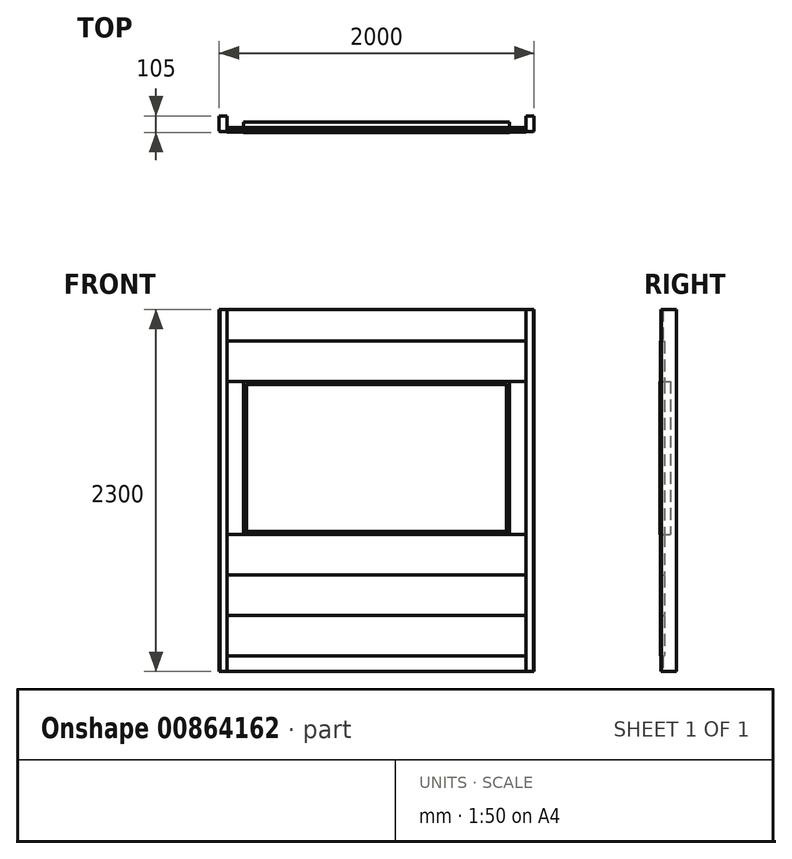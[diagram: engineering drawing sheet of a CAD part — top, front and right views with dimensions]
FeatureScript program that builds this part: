
annotation { "Feature Type Name" : "Feature", "Feature Type Description" : "" }
export const myFeature = defineFeature(function(context is Context, id is Id, definition is map)
    precondition{}
    {
        {
            var Q0;
            Q0=qCreatedBy(makeId("Front.planeOp"),FACE);
            var sketch = newSketch(context, id + "F0", { "sketchPlane" : qUnion([Q0])});
            skLineSegment(sketch, "E0.bottom", {"start": v(-1000, 2300) * mm, "end": v(-950, 2300) * mm});
            skLineSegment(sketch, "E0.top", {"start": v(-1000, 0) * mm, "end": v(-950, 0) * mm});
            skLineSegment(sketch, "E0.left", {"start": v(-1000, 2300) * mm, "end": v(-1000, 0) * mm});
            skLineSegment(sketch, "E0.right", {"start": v(-950, 2300) * mm, "end": v(-950, 0) * mm});
            skLineSegment(sketch, "E1.bottom", {"start": v(950, 2300) * mm, "end": v(1000, 2300) * mm});
            skLineSegment(sketch, "E1.top", {"start": v(950, 0) * mm, "end": v(1000, 0) * mm});
            skLineSegment(sketch, "E1.left", {"start": v(950, 2300) * mm, "end": v(950, 0) * mm});
            skLineSegment(sketch, "E1.right", {"start": v(1000, 2300) * mm, "end": v(1000, 0) * mm});
            skLineSegment(sketch, "E2.bottom", {"start": v(-950, 0) * mm, "end": v(950, 0) * mm});
            skLineSegment(sketch, "E2.top", {"start": v(-950, 100) * mm, "end": v(950, 100) * mm});
            skLineSegment(sketch, "E2.left", {"start": v(-950, 0) * mm, "end": v(-950, 100) * mm});
            skLineSegment(sketch, "E2.right", {"start": v(950, 0) * mm, "end": v(950, 100) * mm});
            skLineSegment(sketch, "E3.bottom", {"start": v(950, 2300) * mm, "end": v(-950, 2300) * mm});
            skLineSegment(sketch, "E3.top", {"start": v(950, 2100) * mm, "end": v(-950, 2100) * mm});
            skLineSegment(sketch, "E3.left", {"start": v(950, 2300) * mm, "end": v(950, 2100) * mm});
            skLineSegment(sketch, "E3.right", {"start": v(-950, 2300) * mm, "end": v(-950, 2100) * mm});
            skLineSegment(sketch, "E4.bottom", {"start": v(-844.5, 1843.25) * mm, "end": v(844.5, 1843.25) * mm});
            skLineSegment(sketch, "E4.top", {"start": v(-844.5, 870.25) * mm, "end": v(844.5, 870.25) * mm});
            skLineSegment(sketch, "E4.left", {"start": v(-844.5, 1843.25) * mm, "end": v(-844.5, 870.25) * mm});
            skLineSegment(sketch, "E4.right", {"start": v(844.5, 1843.25) * mm, "end": v(844.5, 870.25) * mm});
            skLineSegment(sketch, "E5", {"start": v(0, 1843.25) * mm, "end": v(0, 2100) * mm, "construction": true});
            skLineSegment(sketch, "E6", {"start": v(-844.5, 1843.25) * mm, "end": v(-950, 1843.25) * mm});
            skLineSegment(sketch, "E7", {"start": v(844.5, 1843.25) * mm, "end": v(950, 1843.25) * mm});
            skLineSegment(sketch, "E8", {"start": v(-844.5, 870.25) * mm, "end": v(-950, 870.25) * mm});
            skLineSegment(sketch, "E9", {"start": v(844.5, 870.25) * mm, "end": v(950, 870.25) * mm});
            skPoint(sketch, "E9.endSnap0", {"position": v(950, 1150) * mm});
            skLineSegment(sketch, "E10", {"start": v(0, 870.25) * mm, "end": v(0, 613.5) * mm, "construction": true});
            skLineSegment(sketch, "E11", {"start": v(0, 613.5) * mm, "end": v(0, 356.75) * mm, "construction": true});
            skLineSegment(sketch, "E12", {"start": v(0, 356.75) * mm, "end": v(0, 100) * mm, "construction": true});
            skLineSegment(sketch, "E13", {"start": v(-950, 613.5) * mm, "end": v(950, 613.5) * mm});
            skLineSegment(sketch, "E14", {"start": v(-950, 356.75) * mm, "end": v(950, 356.75) * mm});
            skLineSegment(sketch, "E15.bottom", {"start": v(-824.5, 1823.25) * mm, "end": v(824.5, 1823.25) * mm});
            skLineSegment(sketch, "E15.top", {"start": v(-824.5, 890.25) * mm, "end": v(824.5, 890.25) * mm});
            skLineSegment(sketch, "E15.left", {"start": v(-824.5, 1823.25) * mm, "end": v(-824.5, 890.25) * mm});
            skLineSegment(sketch, "E15.right", {"start": v(824.5, 1823.25) * mm, "end": v(824.5, 890.25) * mm});
            skLineSegment(sketch, "E16", {"start": v(0, 1843.25) * mm, "end": v(0, 1823.25) * mm, "construction": true});
            skLineSegment(sketch, "E17", {"start": v(-824.5, 1356.75) * mm, "end": v(-844.5, 1356.75) * mm, "construction": true});
            skSolve(sketch);
        }
        {
            var Q0;
            Q0=makeQuery(id+"F0.imprint","IMPRINT",FACE,{"disambiguationData":[TD([[makeQuery(id+"F0.imprint","IMPRINT",EDGE,{"derivedFrom":sQuery(id+"F0.wireOp",EDGE,"E0.bottom")}),-1.0]])]});
            var Q1;
            Q1=makeQuery(id+"F0.imprint","IMPRINT",FACE,{"disambiguationData":[TD([[makeQuery(id+"F0.imprint","IMPRINT",EDGE,{"derivedFrom":sQuery(id+"F0.wireOp",EDGE,"E1.bottom")}),-1.0]])]});
            extrude(context, id + "F1", {"entities" : qUnion([Q0, Q1]), "oppositeDirection" : true, "depth" : 100 * mm, "offsetDistance" : 25 * mm});
        }
        {
            var Q0;
            Q0=makeQuery(id+"F0.imprint","IMPRINT",FACE,{"disambiguationData":[TD([[makeQuery(id+"F0.imprint","IMPRINT",EDGE,{"derivedFrom":sQuery(id+"F0.wireOp",EDGE,"E3.bottom")}),1.0]])]});
            var Q1;
            Q1=makeQuery(id+"F0.imprint","IMPRINT",FACE,{"disambiguationData":[TD([[makeQuery(id+"F0.imprint","IMPRINT",EDGE,{"derivedFrom":sQuery(id+"F0.wireOp",EDGE,"E2.bottom")}),1.0]])]});
            extrude(context, id + "F2", {"entities" : qUnion([Q0, Q1]), "oppositeDirection" : true, "depth" : 15 * mm, "offsetDistance" : 25 * mm});
        }
        {
            var Q0;
            {var subQ0=sQuery(id+"F0.wireOp",EDGE,"E3.top");Q0=makeQuery(id+"F0.imprint","IMPRINT",FACE,{"disambiguationData":[TD([[makeQuery(id+"F0.imprint","IMPRINT",EDGE,{"derivedFrom":subQ0}),1.0]])]});}
            var Q1;
            Q1=makeQuery(id+"F0.imprint","IMPRINT",FACE,{"disambiguationData":[TD([[makeQuery(id+"F0.imprint","IMPRINT",EDGE,{"derivedFrom":sQuery(id+"F0.wireOp",EDGE,"E4.top")}),-1.0]])]});
            var Q2;
            {var subQ0=sQuery(id+"F0.wireOp",EDGE,"E2.top");Q2=makeQuery(id+"F0.imprint","IMPRINT",FACE,{"disambiguationData":[TD([[makeQuery(id+"F0.imprint","IMPRINT",EDGE,{"derivedFrom":subQ0}),1.0]])]});}
            extrude(context, id + "F3", {"entities" : qUnion([Q0, Q1, Q2]), "depth" : 3 * mm, "offsetDistance" : 25 * mm, "hasSecondDirection" : true, "secondDirectionOppositeDirection" : true, "secondDirectionDepth" : 25 * mm});
        }
        {
            var Q0;
            Q0=makeQuery(id+"F0.imprint","IMPRINT",FACE,{"disambiguationData":[TD([[makeQuery(id+"F0.imprint","IMPRINT",EDGE,{"derivedFrom":sQuery(id+"F0.wireOp",EDGE,"E4.left")}),-1.0]])]});
            var Q1;
            Q1=makeQuery(id+"F0.imprint","IMPRINT",FACE,{"disambiguationData":[TD([[makeQuery(id+"F0.imprint","IMPRINT",EDGE,{"derivedFrom":sQuery(id+"F0.wireOp",EDGE,"E4.right")}),1.0]])]});
            var Q2;
            {var subQ0=sQuery(id+"F0.wireOp",EDGE,"E13");Q2=makeQuery(id+"F0.imprint","IMPRINT",FACE,{"disambiguationData":[TD([[makeQuery(id+"F0.imprint","IMPRINT",EDGE,{"derivedFrom":subQ0}),-1.0]])]});}
            extrude(context, id + "F4", {"entities" : qUnion([Q0, Q1, Q2]), "depth" : 3 * mm, "offsetDistance" : 25 * mm, "hasSecondDirection" : true, "secondDirectionOppositeDirection" : true, "secondDirectionDepth" : 25 * mm});
        }
        {
            var Q0;
            Q0=makeQuery(id+"F0.imprint","IMPRINT",FACE,{"disambiguationData":[TD([[makeQuery(id+"F0.imprint","IMPRINT",EDGE,{"derivedFrom":sQuery(id+"F0.wireOp",EDGE,"E4.bottom")}),-1.0]])]});
            var Q1;
            Q1=makeQuery(id+"F0.imprint","IMPRINT",FACE,{"disambiguationData":[TD([[makeQuery(id+"F0.imprint","IMPRINT",EDGE,{"derivedFrom":sQuery(id+"F0.wireOp",EDGE,"E15.bottom")}),-1.0]])]});
            extrude(context, id + "F5", {"entities" : qUnion([Q0, Q1]), "depth" : 5 * mm, "offsetDistance" : 25 * mm, "hasSecondDirection" : true, "secondDirectionOppositeDirection" : true, "secondDirectionDepth" : 60 * mm});
        }
        {
            var Q0;
            Q0=makeQuery(id+"F0.imprint","IMPRINT",FACE,{"disambiguationData":[TD([[makeQuery(id+"F0.imprint","IMPRINT",EDGE,{"derivedFrom":sQuery(id+"F0.wireOp",EDGE,"E15.bottom")}),-1.0]])]});
            extrude(context, id + "F6", {"entities" : qUnion([Q0]), "operationType" : NewBodyOperationType.REMOVE, "depth" : 25 * mm, "offsetDistance" : 25 * mm});
        }
        {
            var Q0;
            Q0=makeQuery(id+"F6.boolean.opBoolean","INTERSECT",EDGE,{"derivedFrom":[makeQuery(id+"F5.opExtrude","CAP_FACE",FACE,{"disambiguationData":[OSD([sQuery(id+"F0.wireOp",EDGE,"E4.bottom"),sQuery(id+"F0.wireOp",EDGE,"E4.top"),sQuery(id+"F0.wireOp",EDGE,"E4.left"),sQuery(id+"F0.wireOp",EDGE,"E4.right")])],"isStart":false}),makeQuery(id+"F6.opExtrude","SWEPT_FACE",FACE,{"disambiguationData":[OSD([sQuery(id+"F0.wireOp",EDGE,"E15.bottom")])]})]});
            var Q1;
            Q1=makeQuery(id+"F6.boolean.opBoolean","INTERSECT",EDGE,{"derivedFrom":[makeQuery(id+"F5.opExtrude","CAP_FACE",FACE,{"disambiguationData":[OSD([sQuery(id+"F0.wireOp",EDGE,"E4.bottom"),sQuery(id+"F0.wireOp",EDGE,"E4.top"),sQuery(id+"F0.wireOp",EDGE,"E4.left"),sQuery(id+"F0.wireOp",EDGE,"E4.right")])],"isStart":false}),makeQuery(id+"F6.opExtrude","SWEPT_FACE",FACE,{"disambiguationData":[OSD([sQuery(id+"F0.wireOp",EDGE,"E15.left")])]})]});
            var Q2;
            Q2=makeQuery(id+"F6.boolean.opBoolean","INTERSECT",EDGE,{"derivedFrom":[makeQuery(id+"F5.opExtrude","CAP_FACE",FACE,{"disambiguationData":[OSD([sQuery(id+"F0.wireOp",EDGE,"E4.bottom"),sQuery(id+"F0.wireOp",EDGE,"E4.top"),sQuery(id+"F0.wireOp",EDGE,"E4.left"),sQuery(id+"F0.wireOp",EDGE,"E4.right")])],"isStart":false}),makeQuery(id+"F6.opExtrude","SWEPT_FACE",FACE,{"disambiguationData":[OSD([sQuery(id+"F0.wireOp",EDGE,"E15.right")])]})]});
            var Q3;
            Q3=makeQuery(id+"F6.boolean.opBoolean","INTERSECT",EDGE,{"derivedFrom":[makeQuery(id+"F5.opExtrude","CAP_FACE",FACE,{"disambiguationData":[OSD([sQuery(id+"F0.wireOp",EDGE,"E4.bottom"),sQuery(id+"F0.wireOp",EDGE,"E4.top"),sQuery(id+"F0.wireOp",EDGE,"E4.left"),sQuery(id+"F0.wireOp",EDGE,"E4.right")])],"isStart":false}),makeQuery(id+"F6.opExtrude","SWEPT_FACE",FACE,{"disambiguationData":[OSD([sQuery(id+"F0.wireOp",EDGE,"E15.top")])]})]});
            var Q4;
            Q4=makeQuery(id+"F1.opExtrude","CAP_EDGE",EDGE,{"disambiguationData":[OSD([sQuery(id+"F0.wireOp",EDGE,"E0.left")])],"isStart":true});
            var Q5;
            Q5=makeQuery(id+"F1.opExtrude","CAP_EDGE",EDGE,{"disambiguationData":[OSD([sQuery(id+"F0.wireOp",EDGE,"E1.right")])],"isStart":true});
            chamfer(context, id + "F7", {"entities" : qUnion([Q0, Q1, Q2, Q3, Q4, Q5]), "width" : 5 * mm, "tangentPropagation" : true});
        }
        {
            var Q0;
            Q0=makeQuery(id+"F4.opExtrude","CAP_EDGE",EDGE,{"disambiguationData":[OSD([sQuery(id+"F0.wireOp",EDGE,"E4.right")])],"isStart":false});
            var Q1;
            Q1=makeQuery(id+"F3.opExtrude","CAP_EDGE",EDGE,{"disambiguationData":[OSD([sQuery(id+"F0.wireOp",EDGE,"E3.top")])],"isStart":true});
            var Q2;
            Q2=makeQuery(id+"F4.opExtrude","SWEPT_EDGE",EDGE,{"disambiguationData":[OSD([sQuery(id+"F0.wireOp",EDGE,"E4.bottom"),sQuery(id+"F0.wireOp",EDGE,"E4.right"),sQuery(id+"F0.wireOp",EDGE,"E7")])]});
            var Q3;
            Q3=makeQuery(id+"F4.opExtrude","CAP_EDGE",EDGE,{"disambiguationData":[OSD([sQuery(id+"F0.wireOp",EDGE,"E9")])],"isStart":false});
            var Q4;
            Q4=makeQuery(id+"F4.opExtrude","SWEPT_EDGE",EDGE,{"disambiguationData":[OSD([sQuery(id+"F0.wireOp",EDGE,"E4.top"),sQuery(id+"F0.wireOp",EDGE,"E4.right"),sQuery(id+"F0.wireOp",EDGE,"E9")])]});
            var Q5;
            {var subQ0=sQuery(id+"F0.wireOp",EDGE,"E1.left");Q5=makeQuery(id+"F4.opExtrude","CAP_EDGE",EDGE,{"disambiguationData":[OSD([subQ0]),TDD([makeQuery(id+"F0.imprint","IMPRINT",EDGE,{"disambiguationData":[TD([[makeQuery(id+"F0.imprint","INTERSECT",VERTEX,{"derivedFrom":[subQ0,sQuery(id+"F0.wireOp",EDGE,"E7")]}),-1.0]])],"derivedFrom":subQ0})])],"isStart":false});}
            var Q6;
            Q6=makeQuery(id+"F4.opExtrude","SWEPT_EDGE",EDGE,{"disambiguationData":[OSD([sQuery(id+"F0.wireOp",EDGE,"E4.bottom"),sQuery(id+"F0.wireOp",EDGE,"E4.left"),sQuery(id+"F0.wireOp",EDGE,"E6")])]});
            var Q7;
            {var subQ0=sQuery(id+"F0.wireOp",EDGE,"E0.right");Q7=makeQuery(id+"F4.opExtrude","CAP_EDGE",EDGE,{"disambiguationData":[OSD([subQ0]),TDD([makeQuery(id+"F0.imprint","IMPRINT",EDGE,{"disambiguationData":[TD([[makeQuery(id+"F0.imprint","INTERSECT",VERTEX,{"derivedFrom":[subQ0,sQuery(id+"F0.wireOp",EDGE,"E6")]}),-1.0]])],"derivedFrom":subQ0})])],"isStart":false});}
            var Q8;
            Q8=makeQuery(id+"F4.opExtrude","SWEPT_EDGE",EDGE,{"disambiguationData":[OSD([sQuery(id+"F0.wireOp",EDGE,"E4.top"),sQuery(id+"F0.wireOp",EDGE,"E4.left"),sQuery(id+"F0.wireOp",EDGE,"E8")])]});
            var Q9;
            Q9=makeQuery(id+"F4.opExtrude","CAP_EDGE",EDGE,{"disambiguationData":[OSD([sQuery(id+"F0.wireOp",EDGE,"E4.left")])],"isStart":false});
            var Q10;
            Q10=makeQuery(id+"F4.opExtrude","CAP_EDGE",EDGE,{"disambiguationData":[OSD([sQuery(id+"F0.wireOp",EDGE,"E4.left")])],"isStart":true});
            var Q11;
            {var subQ0=sQuery(id+"F0.wireOp",EDGE,"E0.right");Q11=makeQuery(id+"F4.opExtrude","CAP_EDGE",EDGE,{"disambiguationData":[OSD([subQ0]),TDD([makeQuery(id+"F0.imprint","IMPRINT",EDGE,{"disambiguationData":[TD([[makeQuery(id+"F0.imprint","INTERSECT",VERTEX,{"derivedFrom":[subQ0,sQuery(id+"F0.wireOp",EDGE,"E6")]}),-1.0]])],"derivedFrom":subQ0})])],"isStart":true});}
            var Q12;
            Q12=makeQuery(id+"F3.opExtrude","SWEPT_EDGE",EDGE,{"disambiguationData":[OSD([sQuery(id+"F0.wireOp",EDGE,"E1.left"),sQuery(id+"F0.wireOp",EDGE,"E2.top"),sQuery(id+"F0.wireOp",EDGE,"E2.right")])]});
            var Q13;
            {var subQ0=sQuery(id+"F0.wireOp",EDGE,"E0.right");Q13=makeQuery(id+"F3.opExtrude","CAP_EDGE",EDGE,{"disambiguationData":[OSD([subQ0]),TDD([makeQuery(id+"F0.imprint","IMPRINT",EDGE,{"disambiguationData":[TD([[makeQuery(id+"F0.imprint","INTERSECT",VERTEX,{"derivedFrom":[subQ0,sQuery(id+"F0.wireOp",EDGE,"E14")]}),-1.0]])],"derivedFrom":subQ0})])],"isStart":true});}
            var Q14;
            {var subQ0=sQuery(id+"F0.wireOp",EDGE,"E0.right");Q14=makeQuery(id+"F3.opExtrude","CAP_EDGE",EDGE,{"disambiguationData":[OSD([subQ0]),TDD([makeQuery(id+"F0.imprint","IMPRINT",EDGE,{"disambiguationData":[TD([[makeQuery(id+"F0.imprint","INTERSECT",VERTEX,{"derivedFrom":[subQ0,sQuery(id+"F0.wireOp",EDGE,"E14")]}),-1.0]])],"derivedFrom":subQ0})])],"isStart":false});}
            var Q15;
            {var subQ0=sQuery(id+"F0.wireOp",EDGE,"E1.left");Q15=makeQuery(id+"F3.opExtrude","CAP_EDGE",EDGE,{"disambiguationData":[OSD([subQ0]),TDD([makeQuery(id+"F0.imprint","IMPRINT",EDGE,{"disambiguationData":[TD([[makeQuery(id+"F0.imprint","INTERSECT",VERTEX,{"derivedFrom":[subQ0,sQuery(id+"F0.wireOp",EDGE,"E14")]}),-1.0]])],"derivedFrom":subQ0})])],"isStart":true});}
            var Q16;
            {var subQ0=sQuery(id+"F0.wireOp",EDGE,"E1.left");Q16=makeQuery(id+"F3.opExtrude","CAP_EDGE",EDGE,{"disambiguationData":[OSD([subQ0]),TDD([makeQuery(id+"F0.imprint","IMPRINT",EDGE,{"disambiguationData":[TD([[makeQuery(id+"F0.imprint","INTERSECT",VERTEX,{"derivedFrom":[subQ0,sQuery(id+"F0.wireOp",EDGE,"E14")]}),-1.0]])],"derivedFrom":subQ0})])],"isStart":false});}
            var Q17;
            {var subQ0=sQuery(id+"F0.wireOp",EDGE,"E0.right");Q17=makeQuery(id+"F4.opExtrude","CAP_EDGE",EDGE,{"disambiguationData":[OSD([subQ0]),TDD([makeQuery(id+"F0.imprint","IMPRINT",EDGE,{"disambiguationData":[TD([[makeQuery(id+"F0.imprint","INTERSECT",VERTEX,{"derivedFrom":[subQ0,sQuery(id+"F0.wireOp",EDGE,"E13")]}),-1.0]])],"derivedFrom":subQ0})])],"isStart":false});}
            var Q18;
            {var subQ0=sQuery(id+"F0.wireOp",EDGE,"E1.left");Q18=makeQuery(id+"F4.opExtrude","CAP_EDGE",EDGE,{"disambiguationData":[OSD([subQ0]),TDD([makeQuery(id+"F0.imprint","IMPRINT",EDGE,{"disambiguationData":[TD([[makeQuery(id+"F0.imprint","INTERSECT",VERTEX,{"derivedFrom":[subQ0,sQuery(id+"F0.wireOp",EDGE,"E13")]}),-1.0]])],"derivedFrom":subQ0})])],"isStart":false});}
            var Q19;
            {var subQ0=sQuery(id+"F0.wireOp",EDGE,"E0.right");Q19=makeQuery(id+"F3.opExtrude","CAP_EDGE",EDGE,{"disambiguationData":[OSD([subQ0]),TDD([makeQuery(id+"F0.imprint","IMPRINT",EDGE,{"disambiguationData":[TD([[makeQuery(id+"F0.imprint","INTERSECT",VERTEX,{"derivedFrom":[subQ0,sQuery(id+"F0.wireOp",EDGE,"E6")]}),1.0]])],"derivedFrom":subQ0})])],"isStart":false});}
            var Q20;
            Q20=makeQuery(id+"F3.opExtrude","SWEPT_EDGE",EDGE,{"disambiguationData":[OSD([sQuery(id+"F0.wireOp",EDGE,"E1.left"),sQuery(id+"F0.wireOp",EDGE,"E3.top"),sQuery(id+"F0.wireOp",EDGE,"E3.left")])]});
            var Q21;
            {var subQ0=sQuery(id+"F0.wireOp",EDGE,"E0.right");Q21=makeQuery(id+"F3.opExtrude","CAP_EDGE",EDGE,{"disambiguationData":[OSD([subQ0]),TDD([makeQuery(id+"F0.imprint","IMPRINT",EDGE,{"disambiguationData":[TD([[makeQuery(id+"F0.imprint","INTERSECT",VERTEX,{"derivedFrom":[subQ0,sQuery(id+"F0.wireOp",EDGE,"E6")]}),1.0]])],"derivedFrom":subQ0})])],"isStart":true});}
            var Q22;
            Q22=makeQuery(id+"F3.opExtrude","CAP_EDGE",EDGE,{"disambiguationData":[OSD([sQuery(id+"F0.wireOp",EDGE,"E4.bottom"),sQuery(id+"F0.wireOp",EDGE,"E6"),sQuery(id+"F0.wireOp",EDGE,"E7")])],"isStart":false});
            var Q23;
            {var subQ0=sQuery(id+"F0.wireOp",EDGE,"E1.left");Q23=makeQuery(id+"F3.opExtrude","CAP_EDGE",EDGE,{"disambiguationData":[OSD([subQ0]),TDD([makeQuery(id+"F0.imprint","IMPRINT",EDGE,{"disambiguationData":[TD([[makeQuery(id+"F0.imprint","INTERSECT",VERTEX,{"derivedFrom":[subQ0,sQuery(id+"F0.wireOp",EDGE,"E7")]}),1.0]])],"derivedFrom":subQ0})])],"isStart":false});}
            var Q24;
            Q24=makeQuery(id+"F3.opExtrude","CAP_EDGE",EDGE,{"disambiguationData":[OSD([sQuery(id+"F0.wireOp",EDGE,"E3.top")])],"isStart":false});
            var Q25;
            {var subQ0=sQuery(id+"F0.wireOp",EDGE,"E0.right");Q25=makeQuery(id+"F3.opExtrude","CAP_EDGE",EDGE,{"disambiguationData":[OSD([subQ0]),TDD([makeQuery(id+"F0.imprint","IMPRINT",EDGE,{"disambiguationData":[TD([[makeQuery(id+"F0.imprint","INTERSECT",VERTEX,{"derivedFrom":[subQ0,sQuery(id+"F0.wireOp",EDGE,"E8")]}),-1.0]])],"derivedFrom":subQ0})])],"isStart":true});}
            var Q26;
            {var subQ0=sQuery(id+"F0.wireOp",EDGE,"E0.right");Q26=makeQuery(id+"F3.opExtrude","CAP_EDGE",EDGE,{"disambiguationData":[OSD([subQ0]),TDD([makeQuery(id+"F0.imprint","IMPRINT",EDGE,{"disambiguationData":[TD([[makeQuery(id+"F0.imprint","INTERSECT",VERTEX,{"derivedFrom":[subQ0,sQuery(id+"F0.wireOp",EDGE,"E8")]}),-1.0]])],"derivedFrom":subQ0})])],"isStart":false});}
            var Q27;
            Q27=makeQuery(id+"F3.opExtrude","CAP_EDGE",EDGE,{"disambiguationData":[OSD([sQuery(id+"F0.wireOp",EDGE,"E4.top"),sQuery(id+"F0.wireOp",EDGE,"E8"),sQuery(id+"F0.wireOp",EDGE,"E9")])],"isStart":false});
            var Q28;
            {var subQ0=sQuery(id+"F0.wireOp",EDGE,"E1.left");Q28=makeQuery(id+"F3.opExtrude","CAP_EDGE",EDGE,{"disambiguationData":[OSD([subQ0]),TDD([makeQuery(id+"F0.imprint","IMPRINT",EDGE,{"disambiguationData":[TD([[makeQuery(id+"F0.imprint","INTERSECT",VERTEX,{"derivedFrom":[subQ0,sQuery(id+"F0.wireOp",EDGE,"E9")]}),-1.0]])],"derivedFrom":subQ0})])],"isStart":false});}
            var Q29;
            {var subQ0=sQuery(id+"F0.wireOp",EDGE,"E1.left");Q29=makeQuery(id+"F4.opExtrude","CAP_EDGE",EDGE,{"disambiguationData":[OSD([subQ0]),TDD([makeQuery(id+"F0.imprint","IMPRINT",EDGE,{"disambiguationData":[TD([[makeQuery(id+"F0.imprint","INTERSECT",VERTEX,{"derivedFrom":[subQ0,sQuery(id+"F0.wireOp",EDGE,"E7")]}),-1.0]])],"derivedFrom":subQ0})])],"isStart":true});}
            var Q30;
            Q30=makeQuery(id+"F4.opExtrude","CAP_EDGE",EDGE,{"disambiguationData":[OSD([sQuery(id+"F0.wireOp",EDGE,"E7")])],"isStart":false});
            var Q31;
            Q31=makeQuery(id+"F4.opExtrude","SWEPT_EDGE",EDGE,{"disambiguationData":[OSD([sQuery(id+"F0.wireOp",EDGE,"E1.left"),sQuery(id+"F0.wireOp",EDGE,"E7")])]});
            var Q32;
            Q32=makeQuery(id+"F4.opExtrude","CAP_EDGE",EDGE,{"disambiguationData":[OSD([sQuery(id+"F0.wireOp",EDGE,"E4.right")])],"isStart":true});
            var Q33;
            Q33=makeQuery(id+"F4.opExtrude","SWEPT_EDGE",EDGE,{"disambiguationData":[OSD([sQuery(id+"F0.wireOp",EDGE,"E1.left"),sQuery(id+"F0.wireOp",EDGE,"E9")])]});
            var Q34;
            Q34=makeQuery(id+"F4.opExtrude","CAP_EDGE",EDGE,{"disambiguationData":[OSD([sQuery(id+"F0.wireOp",EDGE,"E9")])],"isStart":true});
            var Q35;
            Q35=makeQuery(id+"F4.opExtrude","CAP_EDGE",EDGE,{"disambiguationData":[OSD([sQuery(id+"F0.wireOp",EDGE,"E8")])],"isStart":false});
            var Q36;
            Q36=makeQuery(id+"F4.opExtrude","SWEPT_EDGE",EDGE,{"disambiguationData":[OSD([sQuery(id+"F0.wireOp",EDGE,"E0.right"),sQuery(id+"F0.wireOp",EDGE,"E8")])]});
            var Q37;
            Q37=makeQuery(id+"F4.opExtrude","CAP_EDGE",EDGE,{"disambiguationData":[OSD([sQuery(id+"F0.wireOp",EDGE,"E6")])],"isStart":false});
            var Q38;
            Q38=makeQuery(id+"F4.opExtrude","SWEPT_EDGE",EDGE,{"disambiguationData":[OSD([sQuery(id+"F0.wireOp",EDGE,"E0.right"),sQuery(id+"F0.wireOp",EDGE,"E6")])]});
            var Q39;
            Q39=makeQuery(id+"F3.opExtrude","SWEPT_EDGE",EDGE,{"disambiguationData":[OSD([sQuery(id+"F0.wireOp",EDGE,"E0.right"),sQuery(id+"F0.wireOp",EDGE,"E2.top"),sQuery(id+"F0.wireOp",EDGE,"E2.left")])]});
            var Q40;
            Q40=makeQuery(id+"F3.opExtrude","CAP_EDGE",EDGE,{"disambiguationData":[OSD([sQuery(id+"F0.wireOp",EDGE,"E2.top")])],"isStart":false});
            var Q41;
            Q41=makeQuery(id+"F4.opExtrude","CAP_EDGE",EDGE,{"disambiguationData":[OSD([sQuery(id+"F0.wireOp",EDGE,"E14")])],"isStart":false});
            var Q42;
            Q42=makeQuery(id+"F4.opExtrude","CAP_EDGE",EDGE,{"disambiguationData":[OSD([sQuery(id+"F0.wireOp",EDGE,"E13")])],"isStart":false});
            var Q43;
            Q43=makeQuery(id+"F4.opExtrude","SWEPT_EDGE",EDGE,{"disambiguationData":[OSD([sQuery(id+"F0.wireOp",EDGE,"E1.left"),sQuery(id+"F0.wireOp",EDGE,"E14")])]});
            var Q44;
            Q44=makeQuery(id+"F4.opExtrude","SWEPT_EDGE",EDGE,{"disambiguationData":[OSD([sQuery(id+"F0.wireOp",EDGE,"E0.right"),sQuery(id+"F0.wireOp",EDGE,"E13")])]});
            var Q45;
            Q45=makeQuery(id+"F4.opExtrude","CAP_EDGE",EDGE,{"disambiguationData":[OSD([sQuery(id+"F0.wireOp",EDGE,"E13")])],"isStart":true});
            var Q46;
            {var subQ0=sQuery(id+"F0.wireOp",EDGE,"E1.left");Q46=makeQuery(id+"F4.opExtrude","CAP_EDGE",EDGE,{"disambiguationData":[OSD([subQ0]),TDD([makeQuery(id+"F0.imprint","IMPRINT",EDGE,{"disambiguationData":[TD([[makeQuery(id+"F0.imprint","INTERSECT",VERTEX,{"derivedFrom":[subQ0,sQuery(id+"F0.wireOp",EDGE,"E13")]}),-1.0]])],"derivedFrom":subQ0})])],"isStart":true});}
            var Q47;
            {var subQ0=sQuery(id+"F0.wireOp",EDGE,"E0.right");Q47=makeQuery(id+"F4.opExtrude","CAP_EDGE",EDGE,{"disambiguationData":[OSD([subQ0]),TDD([makeQuery(id+"F0.imprint","IMPRINT",EDGE,{"disambiguationData":[TD([[makeQuery(id+"F0.imprint","INTERSECT",VERTEX,{"derivedFrom":[subQ0,sQuery(id+"F0.wireOp",EDGE,"E13")]}),-1.0]])],"derivedFrom":subQ0})])],"isStart":true});}
            var Q48;
            Q48=makeQuery(id+"F4.opExtrude","SWEPT_EDGE",EDGE,{"disambiguationData":[OSD([sQuery(id+"F0.wireOp",EDGE,"E1.left"),sQuery(id+"F0.wireOp",EDGE,"E13")])]});
            var Q49;
            Q49=makeQuery(id+"F4.opExtrude","SWEPT_EDGE",EDGE,{"disambiguationData":[OSD([sQuery(id+"F0.wireOp",EDGE,"E0.right"),sQuery(id+"F0.wireOp",EDGE,"E14")])]});
            var Q50;
            Q50=makeQuery(id+"F4.opExtrude","CAP_EDGE",EDGE,{"disambiguationData":[OSD([sQuery(id+"F0.wireOp",EDGE,"E14")])],"isStart":true});
            var Q51;
            Q51=makeQuery(id+"F3.opExtrude","SWEPT_EDGE",EDGE,{"disambiguationData":[OSD([sQuery(id+"F0.wireOp",EDGE,"E0.right"),sQuery(id+"F0.wireOp",EDGE,"E3.top"),sQuery(id+"F0.wireOp",EDGE,"E3.right")])]});
            var Q52;
            {var subQ0=sQuery(id+"F0.wireOp",EDGE,"E1.left");Q52=makeQuery(id+"F3.opExtrude","CAP_EDGE",EDGE,{"disambiguationData":[OSD([subQ0]),TDD([makeQuery(id+"F0.imprint","IMPRINT",EDGE,{"disambiguationData":[TD([[makeQuery(id+"F0.imprint","INTERSECT",VERTEX,{"derivedFrom":[subQ0,sQuery(id+"F0.wireOp",EDGE,"E7")]}),1.0]])],"derivedFrom":subQ0})])],"isStart":true});}
            var Q53;
            Q53=makeQuery(id+"F3.opExtrude","CAP_EDGE",EDGE,{"disambiguationData":[OSD([sQuery(id+"F0.wireOp",EDGE,"E4.bottom"),sQuery(id+"F0.wireOp",EDGE,"E6"),sQuery(id+"F0.wireOp",EDGE,"E7")])],"isStart":true});
            var Q54;
            Q54=makeQuery(id+"F3.opExtrude","CAP_EDGE",EDGE,{"disambiguationData":[OSD([sQuery(id+"F0.wireOp",EDGE,"E4.top"),sQuery(id+"F0.wireOp",EDGE,"E8"),sQuery(id+"F0.wireOp",EDGE,"E9")])],"isStart":true});
            var Q55;
            {var subQ0=sQuery(id+"F0.wireOp",EDGE,"E1.left");Q55=makeQuery(id+"F3.opExtrude","CAP_EDGE",EDGE,{"disambiguationData":[OSD([subQ0]),TDD([makeQuery(id+"F0.imprint","IMPRINT",EDGE,{"disambiguationData":[TD([[makeQuery(id+"F0.imprint","INTERSECT",VERTEX,{"derivedFrom":[subQ0,sQuery(id+"F0.wireOp",EDGE,"E9")]}),-1.0]])],"derivedFrom":subQ0})])],"isStart":true});}
            var Q56;
            Q56=makeQuery(id+"F4.opExtrude","CAP_EDGE",EDGE,{"disambiguationData":[OSD([sQuery(id+"F0.wireOp",EDGE,"E7")])],"isStart":true});
            var Q57;
            Q57=makeQuery(id+"F4.opExtrude","CAP_EDGE",EDGE,{"disambiguationData":[OSD([sQuery(id+"F0.wireOp",EDGE,"E6")])],"isStart":true});
            var Q58;
            Q58=makeQuery(id+"F4.opExtrude","CAP_EDGE",EDGE,{"disambiguationData":[OSD([sQuery(id+"F0.wireOp",EDGE,"E8")])],"isStart":true});
            var Q59;
            Q59=makeQuery(id+"F3.opExtrude","SWEPT_EDGE",EDGE,{"disambiguationData":[OSD([sQuery(id+"F0.wireOp",EDGE,"E0.right"),sQuery(id+"F0.wireOp",EDGE,"E14")])]});
            var Q60;
            Q60=makeQuery(id+"F3.opExtrude","SWEPT_EDGE",EDGE,{"disambiguationData":[OSD([sQuery(id+"F0.wireOp",EDGE,"E1.left"),sQuery(id+"F0.wireOp",EDGE,"E14")])]});
            var Q61;
            Q61=makeQuery(id+"F3.opExtrude","CAP_EDGE",EDGE,{"disambiguationData":[OSD([sQuery(id+"F0.wireOp",EDGE,"E14")])],"isStart":true});
            var Q62;
            Q62=makeQuery(id+"F3.opExtrude","CAP_EDGE",EDGE,{"disambiguationData":[OSD([sQuery(id+"F0.wireOp",EDGE,"E14")])],"isStart":false});
            var Q63;
            Q63=makeQuery(id+"F3.opExtrude","CAP_EDGE",EDGE,{"disambiguationData":[OSD([sQuery(id+"F0.wireOp",EDGE,"E2.top")])],"isStart":true});
            var Q64;
            Q64=makeQuery(id+"F3.opExtrude","SWEPT_EDGE",EDGE,{"disambiguationData":[OSD([sQuery(id+"F0.wireOp",EDGE,"E0.right"),sQuery(id+"F0.wireOp",EDGE,"E6")])]});
            var Q65;
            Q65=makeQuery(id+"F3.opExtrude","SWEPT_EDGE",EDGE,{"disambiguationData":[OSD([sQuery(id+"F0.wireOp",EDGE,"E1.left"),sQuery(id+"F0.wireOp",EDGE,"E7")])]});
            var Q66;
            Q66=makeQuery(id+"F3.opExtrude","SWEPT_EDGE",EDGE,{"disambiguationData":[OSD([sQuery(id+"F0.wireOp",EDGE,"E0.right"),sQuery(id+"F0.wireOp",EDGE,"E8")])]});
            var Q67;
            Q67=makeQuery(id+"F3.opExtrude","SWEPT_EDGE",EDGE,{"disambiguationData":[OSD([sQuery(id+"F0.wireOp",EDGE,"E1.left"),sQuery(id+"F0.wireOp",EDGE,"E9")])]});
            var Q68;
            Q68=makeQuery(id+"F3.opExtrude","SWEPT_EDGE",EDGE,{"disambiguationData":[OSD([sQuery(id+"F0.wireOp",EDGE,"E0.right"),sQuery(id+"F0.wireOp",EDGE,"E13")])]});
            var Q69;
            Q69=makeQuery(id+"F3.opExtrude","SWEPT_EDGE",EDGE,{"disambiguationData":[OSD([sQuery(id+"F0.wireOp",EDGE,"E1.left"),sQuery(id+"F0.wireOp",EDGE,"E13")])]});
            var Q70;
            Q70=makeQuery(id+"F3.opExtrude","CAP_EDGE",EDGE,{"disambiguationData":[OSD([sQuery(id+"F0.wireOp",EDGE,"E13")])],"isStart":true});
            var Q71;
            Q71=makeQuery(id+"F3.opExtrude","CAP_EDGE",EDGE,{"disambiguationData":[OSD([sQuery(id+"F0.wireOp",EDGE,"E13")])],"isStart":false});
            fillet(context, id + "F8", {"entities" : qUnion([Q0, Q1, Q2, Q3, Q4, Q5, Q6, Q7, Q8, Q9, Q10, Q11, Q12, Q13, Q14, Q15, Q16, Q17, Q18, Q19, Q20, Q21, Q22, Q23, Q24, Q25, Q26, Q27, Q28, Q29, Q30, Q31, Q32, Q33, Q34, Q35, Q36, Q37, Q38, Q39, Q40, Q41, Q42, Q43, Q44, Q45, Q46, Q47, Q48, Q49, Q50, Q51, Q52, Q53, Q54, Q55, Q56, Q57, Q58, Q59, Q60, Q61, Q62, Q63, Q64, Q65, Q66, Q67, Q68, Q69, Q70, Q71]), "radius" : 3 * mm, "tangentPropagation" : true, "allowEdgeOverflow" : false});
        }
    });
